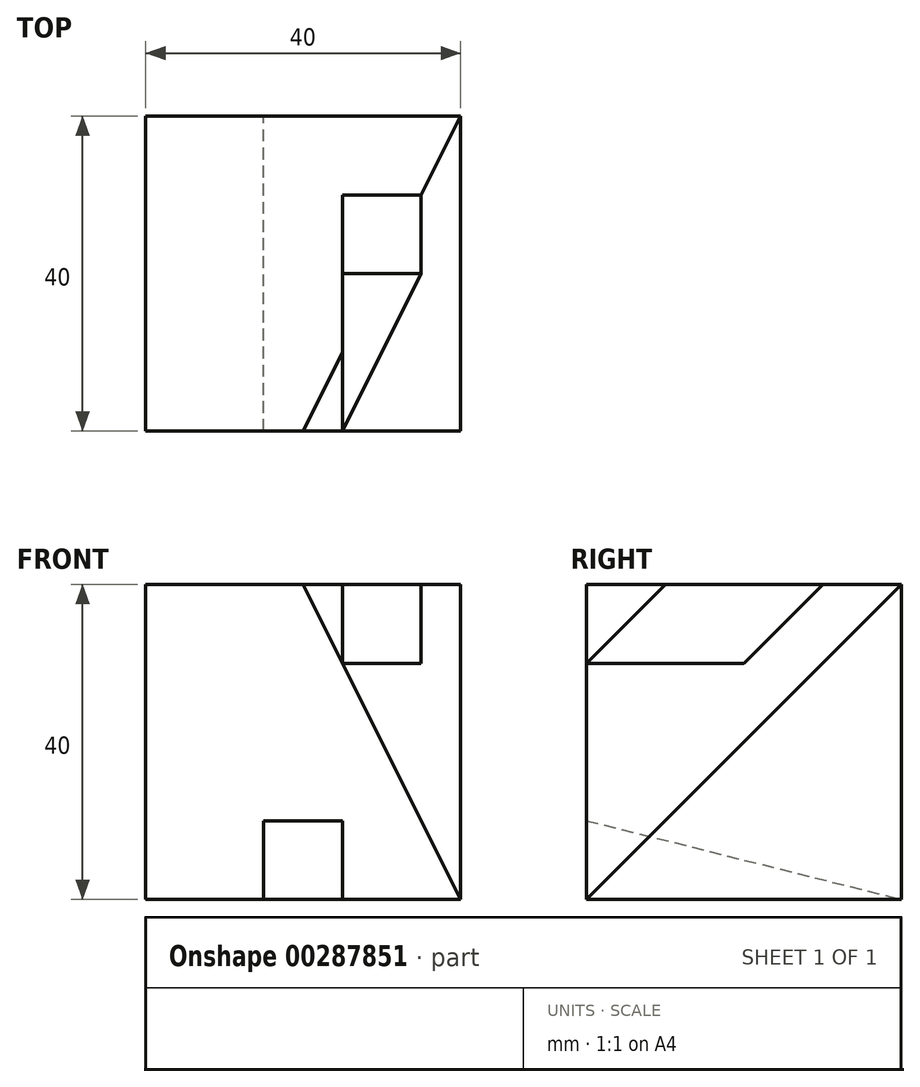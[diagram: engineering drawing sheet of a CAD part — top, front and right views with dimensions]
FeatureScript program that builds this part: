
annotation { "Feature Type Name" : "Feature", "Feature Type Description" : "" }
export const myFeature = defineFeature(function(context is Context, id is Id, definition is map)
    precondition{}
    {
        {
            var Q0;
            Q0=qCreatedBy(makeId("Right.planeOp"),FACE);
            var sketch = newSketch(context, id + "F0", { "sketchPlane" : qUnion([Q0])});
            skLineSegment(sketch, "E0.bottom", {"start": v(0, 0) * mm, "end": v(40, 0) * mm});
            skLineSegment(sketch, "E0.top", {"start": v(0, 40) * mm, "end": v(40, 40) * mm});
            skLineSegment(sketch, "E0.left", {"start": v(0, 0) * mm, "end": v(0, 40) * mm});
            skLineSegment(sketch, "E0.right", {"start": v(40, 0) * mm, "end": v(40, 40) * mm});
            skSolve(sketch);
        }
        {
            var Q0;
            Q0 = qSketchRegion(id + "F0", true);
            extrude(context, id + "F1", {"entities" : qUnion([Q0]), "depth" : 40 * mm, "symmetric" : true});
        }
        {
            var Q0;
            Q0=makeQuery(id+"F1.opExtrude","SWEPT_EDGE",EDGE,{"disambiguationData":[OSD([sQuery(id+"F0.wireOp",EDGE,"E0.top"),sQuery(id+"F0.wireOp",EDGE,"E0.left")])]});
            cPoint(context, id + "F2", {"entities" : qUnion([Q0]), "parameter" : 0.5});
        }
        {
            var Q0;
            Q0=makeQuery(id+"F1.opExtrude","CAP_VERTEX",VERTEX,{"disambiguationData":[OSD([sQuery(id+"F0.wireOp",EDGE,"E0.top"),sQuery(id+"F0.wireOp",EDGE,"E0.right")])],"isStart":false});
            var Q1;
            Q1 = qCreatedBy(id + "F2" ,VERTEX);
            var Q2;
            Q2=makeQuery(id+"F1.opExtrude","CAP_VERTEX",VERTEX,{"disambiguationData":[OSD([sQuery(id+"F0.wireOp",EDGE,"E0.bottom"),sQuery(id+"F0.wireOp",EDGE,"E0.left")])],"isStart":false});
            cPlane(context, id + "F3", {"entities" : qUnion([Q0, Q1, Q2]), "cplaneType" : CPlaneType.THREE_POINT, "offset" : 25 * mm, "width" : 150 * mm, "height" : 150 * mm});
        }
        {
            var Q0;
            Q0=qCreatedBy(id+"F3.planeOp",FACE);
            var sketch = newSketch(context, id + "F4", { "sketchPlane" : qUnion([Q0])});
            skPoint(sketch, "E1.0", {"position": v(-7.3, 35.78) * mm});
            skPoint(sketch, "E2.0", {"position": v(-51.12, 26.83) * mm});
            skPoint(sketch, "E3.0", {"position": v(-7.3, -8.94) * mm});
            skLineSegment(sketch, "E4", {"start": v(-7.3, 35.78) * mm, "end": v(-51.12, 26.83) * mm});
            skLineSegment(sketch, "E5", {"start": v(-7.3, -8.94) * mm, "end": v(-7.3, 35.78) * mm});
            skLineSegment(sketch, "E6", {"start": v(-7.3, -8.94) * mm, "end": v(-51.12, 26.83) * mm});
            skSolve(sketch);
        }
        {
            var Q0;
            Q0 = qSketchRegion(id + "F4", true);
            extrude(context, id + "F5", {"entities" : qUnion([Q0]), "operationType" : NewBodyOperationType.REMOVE, "endBound" : BoundingType.THROUGH_ALL, "oppositeDirection" : true, "depth" : 25 * mm});
        }
        {
            var Q0;
            Q0=qCreatedBy(makeId("Right.planeOp"),FACE);
            var sketch = newSketch(context, id + "F6", { "sketchPlane" : qUnion([Q0])});
            skLineSegment(sketch, "E7.0", {"start": v(0, 0) * mm, "end": v(0, 40) * mm});
            skLineSegment(sketch, "E8.0", {"start": v(0, 0) * mm, "end": v(40, 0) * mm});
            skLineSegment(sketch, "E9", {"start": v(0, 10) * mm, "end": v(40, 0) * mm});
            skSolve(sketch);
        }
        {
            var Q0;
            Q0 = qSketchRegion(id + "F6", true);
            extrude(context, id + "F7", {"entities" : qUnion([Q0]), "operationType" : NewBodyOperationType.REMOVE, "depth" : 10 * mm, "symmetric" : true});
        }
        {
            var Q0;
            Q0=makeQuery(id+"F1.opExtrude","CAP_FACE",FACE,{"disambiguationData":[OSD([sQuery(id+"F0.wireOp",EDGE,"E0.bottom"),sQuery(id+"F0.wireOp",EDGE,"E0.top"),sQuery(id+"F0.wireOp",EDGE,"E0.left"),sQuery(id+"F0.wireOp",EDGE,"E0.right")])],"isStart":false});
            var sketch = newSketch(context, id + "F8", { "sketchPlane" : qUnion([Q0])});
            skLineSegment(sketch, "E10.0", {"start": v(0, 40) * mm, "end": v(40, 40) * mm});
            skLineSegment(sketch, "E11.0", {"start": v(0, 0) * mm, "end": v(0, 40) * mm});
            skLineSegment(sketch, "E12.0", {"start": v(0, 0) * mm, "end": v(40, 40) * mm});
            skLineSegment(sketch, "E13", {"start": v(30, 40) * mm, "end": v(20, 30) * mm});
            skPoint(sketch, "E13.endSnap0", {"position": v(20, 40) * mm});
            skLineSegment(sketch, "E14", {"start": v(20, 30) * mm, "end": v(0, 30) * mm});
            skLineSegment(sketch, "E15", {"start": v(0, 30) * mm, "end": v(10, 40) * mm});
            skSolve(sketch);
        }
        {
            var Q0;
            {var subQ0=sQuery(id+"F8.wireOp",EDGE,"E13");Q0=makeQuery(id+"F8.imprint","IMPRINT",FACE,{"disambiguationData":[TD([[makeQuery(id+"F8.imprint","IMPRINT",EDGE,{"derivedFrom":subQ0}),-1.0]])]});}
            extrude(context, id + "F9", {"entities" : qUnion([Q0]), "operationType" : NewBodyOperationType.REMOVE, "oppositeDirection" : true, "depth" : 15 * mm});
        }
    });
